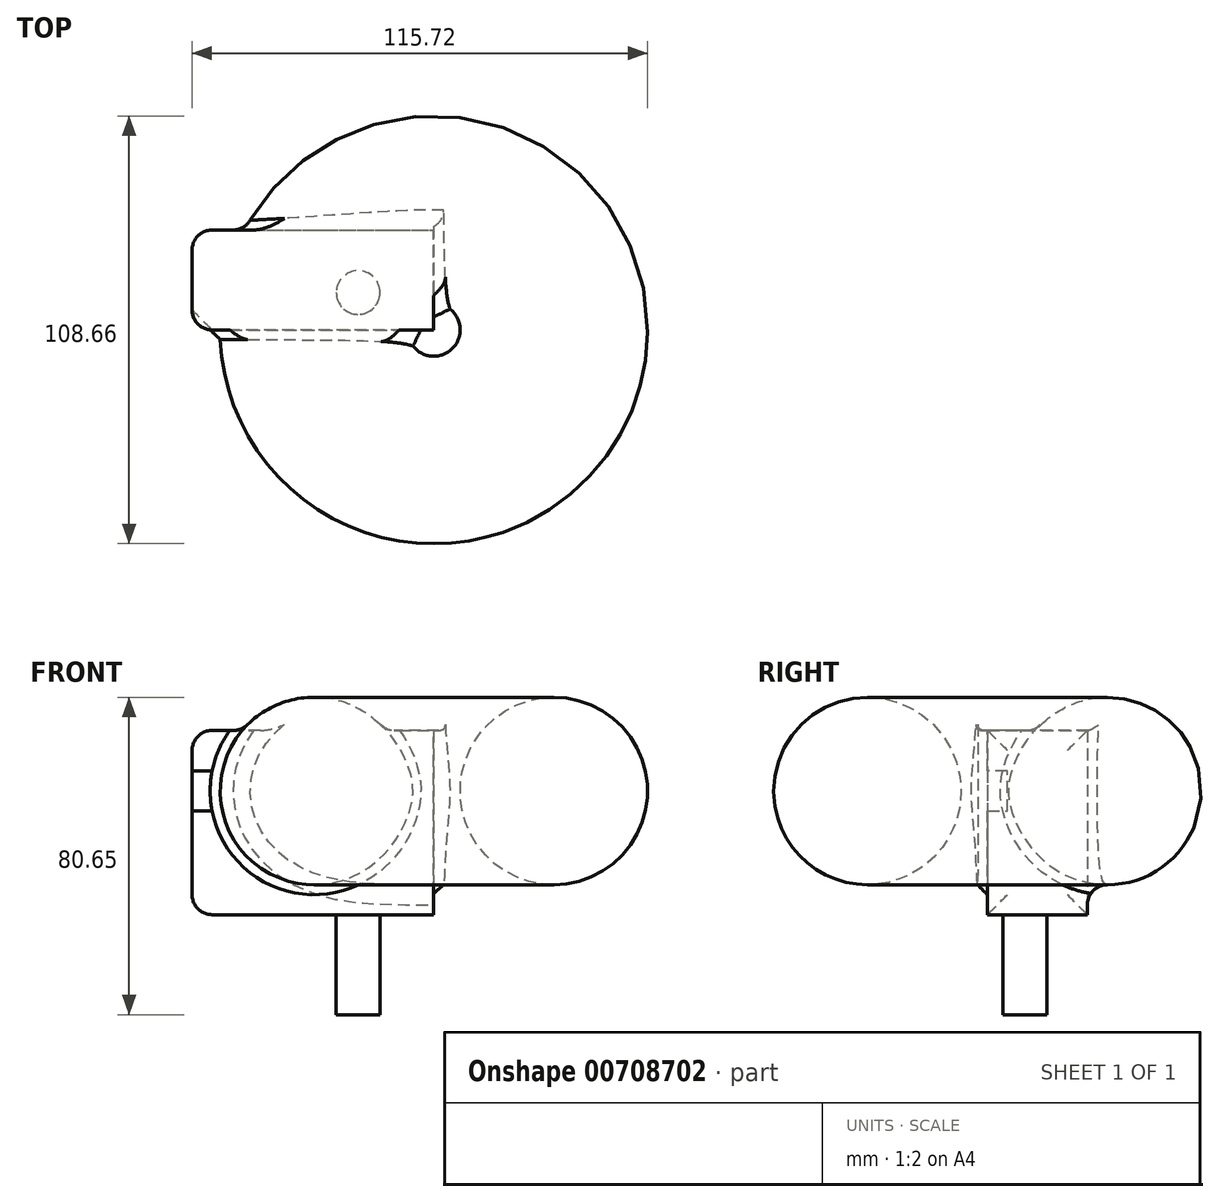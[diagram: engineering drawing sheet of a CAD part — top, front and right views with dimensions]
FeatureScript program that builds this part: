
annotation { "Feature Type Name" : "Feature", "Feature Type Description" : "" }
export const myFeature = defineFeature(function(context is Context, id is Id, definition is map)
    precondition{}
    {
        {
            var Q0;
            Q0=qCreatedBy(makeId("Front.planeOp"),FACE);
            var sketch = newSketch(context, id + "F0", { "sketchPlane" : qUnion([Q0])});
            skLineSegment(sketch, "E0.bottom", {"start": v(-16.5, 15.4) * mm, "end": v(44.9, 15.4) * mm});
            skLineSegment(sketch, "E0.top", {"start": v(-16.5, -31.43) * mm, "end": v(44.9, -31.43) * mm});
            skLineSegment(sketch, "E0.left", {"start": v(-16.5, 15.4) * mm, "end": v(-16.5, -31.43) * mm});
            skLineSegment(sketch, "E0.right", {"start": v(44.9, 15.4) * mm, "end": v(44.9, -31.43) * mm});
            skSolve(sketch);
        }
        {
            var Q0;
            Q0 = qSketchRegion(id + "F0", true);
            extrude(context, id + "F1", {"entities" : qUnion([Q0]), "depth" : 25.4 * mm, "offsetDistance" : 25.4 * mm});
        }
        {
            var Q0;
            Q0=makeQuery(id+"F1.opExtrude","CAP_FACE",FACE,{"disambiguationData":[OSD([sQuery(id+"F0.wireOp",EDGE,"E0.bottom"),sQuery(id+"F0.wireOp",EDGE,"E0.top"),sQuery(id+"F0.wireOp",EDGE,"E0.left"),sQuery(id+"F0.wireOp",EDGE,"E0.right")])],"isStart":false});
            var sketch = newSketch(context, id + "F2", { "sketchPlane" : qUnion([Q0])});
            skCircle(sketch, "E1", {"center": v(14.38, 0) * mm, "radius": 23.82 * mm});
            skSolve(sketch);
        }
        {
            var Q0;
            Q0 = qSketchRegion(id + "F2", true);
            var Q1;
            Q1=makeQuery(id+"F1.opExtrude","CAP_EDGE",EDGE,{"disambiguationData":[OSD([sQuery(id+"F0.wireOp",EDGE,"E0.right")])],"isStart":false});
            revolve(context, id + "F3", {"operationType" : NewBodyOperationType.ADD, "surfaceOperationType" : NewSurfaceOperationType.NEW, "entities" : qUnion([Q0]), "axis" : qUnion([Q1]), "revolveType" : RevolveType.FULL});
        }
        {
            var Q0;
            Q0=makeQuery(id+"F3.boolean.opBoolean","INTERSECT",EDGE,{"derivedFrom":[makeQuery(id+"F1.opExtrude","CAP_FACE",FACE,{"disambiguationData":[OSD([sQuery(id+"F0.wireOp",EDGE,"E0.bottom"),sQuery(id+"F0.wireOp",EDGE,"E0.top"),sQuery(id+"F0.wireOp",EDGE,"E0.left"),sQuery(id+"F0.wireOp",EDGE,"E0.right")])],"isStart":true}),makeQuery(id+"F3.opRevolve","SWEPT_FACE",FACE,{"disambiguationData":[OSD([sQuery(id+"F2.wireOp",EDGE,"E1")])]})]});
            var Q1;
            Q1=makeQuery(id+"F3.boolean.opBoolean","INTERSECT",EDGE,{"disambiguationData":[OD(1.0)],"derivedFrom":[makeQuery(id+"F1.opExtrude","SWEPT_FACE",FACE,{"disambiguationData":[OSD([sQuery(id+"F0.wireOp",EDGE,"E0.bottom")])]}),makeQuery(id+"F3.opRevolve","SWEPT_FACE",FACE,{"disambiguationData":[OSD([sQuery(id+"F2.wireOp",EDGE,"E1")])]})]});
            var Q2;
            Q2=makeQuery(id+"F3.boolean.opBoolean","INTERSECT",EDGE,{"disambiguationData":[OD(0.0)],"derivedFrom":[makeQuery(id+"F1.opExtrude","SWEPT_FACE",FACE,{"disambiguationData":[OSD([sQuery(id+"F0.wireOp",EDGE,"E0.bottom")])]}),makeQuery(id+"F3.opRevolve","SWEPT_FACE",FACE,{"disambiguationData":[OSD([sQuery(id+"F2.wireOp",EDGE,"E1")])]})]});
            fillet(context, id + "F4", {"entities" : qUnion([Q0, Q1, Q2]), "radius" : 5.08 * mm, "tangentPropagation" : true, "allowEdgeOverflow" : false});
        }
        {
            var Q0;
            Q0=makeQuery(id+"F3.boolean.opBoolean","INTERSECT",EDGE,{"derivedFrom":[makeQuery(id+"F1.opExtrude","CAP_FACE",FACE,{"disambiguationData":[OSD([sQuery(id+"F0.wireOp",EDGE,"E0.bottom"),sQuery(id+"F0.wireOp",EDGE,"E0.top"),sQuery(id+"F0.wireOp",EDGE,"E0.left"),sQuery(id+"F0.wireOp",EDGE,"E0.right")])],"isStart":false}),makeQuery(id+"F3.opRevolve","SWEPT_FACE",FACE,{"disambiguationData":[OSD([sQuery(id+"F2.wireOp",EDGE,"E1")])]})]});
            var Q1;
            Q1=makeQuery(id+"F3.boolean.opBoolean","INTERSECT",EDGE,{"derivedFrom":[makeQuery(id+"F1.opExtrude","SWEPT_FACE",FACE,{"disambiguationData":[OSD([sQuery(id+"F0.wireOp",EDGE,"E0.right")])]}),makeQuery(id+"F3.opRevolve","SWEPT_FACE",FACE,{"disambiguationData":[OSD([sQuery(id+"F2.wireOp",EDGE,"E1")])]})]});
            chamfer(context, id + "F5", {"entities" : qUnion([Q0, Q1]), "width" : 2.54 * mm, "tangentPropagation" : true});
        }
        {
            var Q0;
            Q0=makeQuery(id+"F1.opExtrude","SWEPT_FACE",FACE,{"disambiguationData":[OSD([sQuery(id+"F0.wireOp",EDGE,"E0.left")])]});
            fillet(context, id + "F6", {"entities" : qUnion([Q0]), "radius" : 5.08 * mm, "tangentPropagation" : true, "allowEdgeOverflow" : false});
        }
        {
            var Q0;
            Q0=makeQuery(id+"F1.opExtrude","SWEPT_FACE",FACE,{"disambiguationData":[OSD([sQuery(id+"F0.wireOp",EDGE,"E0.top")])]});
            var sketch = newSketch(context, id + "F7", { "sketchPlane" : qUnion([Q0])});
            skCircle(sketch, "E2", {"center": v(25.67, 15.9) * mm, "radius": 5.55 * mm});
            skSolve(sketch);
        }
        {
            var Q0;
            Q0 = qSketchRegion(id + "F7", true);
            extrude(context, id + "F8", {"entities" : qUnion([Q0]), "operationType" : NewBodyOperationType.ADD, "depth" : 25.4 * mm, "offsetDistance" : 25.4 * mm});
        }
    });
